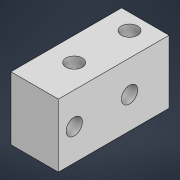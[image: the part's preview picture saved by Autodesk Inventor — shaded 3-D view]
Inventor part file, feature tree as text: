
AUTODESK INVENTOR PART (.ipt)
format: ipt  version: 2022.2 (Build 262287000, 287)  size: 129,024 bytes
history: native  units: in
note: dims shown in document units (in); Inventor stores cm internally (conversion verified against a paired STEP export)
features: sketch x5, hole x4, extrude x1
ambient origin geometry x8: Origin, YZ Plane, XZ Plane, XY Plane, X Axis, Y Axis, Z Axis, Center Point
bodies: Solid1 (feature_tree)
feature tree (10):
  extrude  "Extrusion1"  Depth=1.75in
  hole  "Hole1"  [1 undecoded]
  hole  "Hole2"  [1 undecoded]
  sketch  "Sketch4"  dims[d7=0.375in]
  hole  "Hole3"  [1 undecoded]
  hole  "Hole4"  [1 undecoded]
  sketch  "Sketch1"  dims[d0=0.75in d1=1.75in]
  sketch  "Sketch2"  dims[d2=1.0in d3=0.0in d4=0.5in]
  sketch  "Sketch3"  dims[d5=0.5in d6=0.25in]
  sketch  "Sketch5"  dims[d8=0.257in d9=0.75in d10=0.375in d11=0.25in d12=0.5635in d13=2.0in d14=0.8108in d15=0.375in d16=0.625in d17=0.257in d18=0.75in d19=0.375in d20=0.25in d21=0.5635in d22=2.0in d23=0.8108in d24=0.5in d25=1.125in d26=0.375in d27=0.25in d28=0.257in d29=0.75in d30=0.375in d31=0.25in d32=0.5635in d33=2.0in d34=0.8108in d35=0.257in d36=0.75in d37=0.375in d38=0.25in d39=0.5635in d40=2.0in d41=0.8108in]
note: 4 required parameter values undecoded (feature->parameter linkage not recoverable at this tier; creation-order binding heuristic only, values carry confidence <= 0.55)
